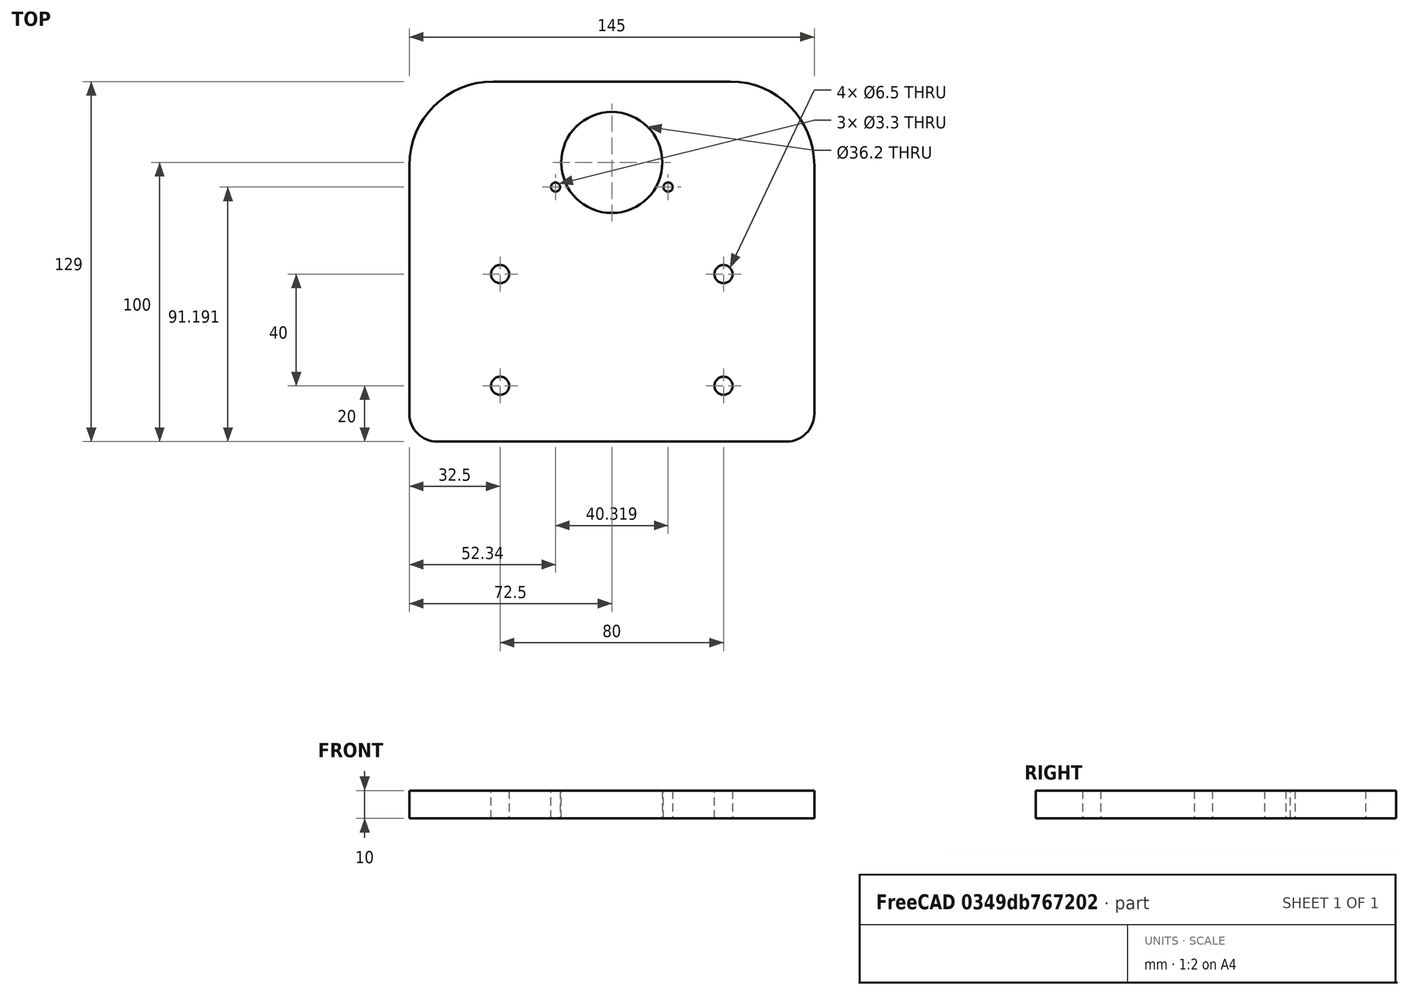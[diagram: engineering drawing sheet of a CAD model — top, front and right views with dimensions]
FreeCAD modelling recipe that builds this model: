
FCSTD DOCUMENT  (FreeCAD 0.21R38887 (Git))
Label: ПластинаY
License: All rights reserved
LicenseURL: http://en.wikipedia.org/wiki/All_rights_reserved
objects: App::Link×2, Sketcher::SketchObject×1, PartDesign::Pad×1, PartDesign::Body×1
note: 6 computed .brp shape members not serialized (recipe doc carries the construction recipe); baked Part::Feature solids carry a one-line shape summary decoded from their .brp
EXTERNAL_REF file=../../../ТаблицаПараметров.FCStd obj=Spreadsheet
EXTERNAL_REF file=../../../ТаблицаПараметров.FCStd obj=Spreadsheet007

FEATURE [Sketcher::SketchObject] Sketch001
  ArcFitTolerance = 0
  ExternalBSplineMaxDegree = 0
  ExternalBSplineTolerance = 0
  FullyConstrained = false
  InternalTolerance = 1e-06
  InvalidShape = false
  MakeInternals = false
  TreeRank = 235
  ValidateShape = false
  expr: Constraints[0] = <<Link(ПластиныY)>>.Len1
  expr: Constraints[1] = <<Link(ПластиныY)>>.Heigh1
  expr: Constraints[38] = <<Link(ПластиныY)>>.Heigh2
  expr: Constraints[48] = <<Link001(Профиль)>>.HTpaz1
  expr: Constraints[49] = <<Link001(Профиль)>>.HTpaz2
  sketch-geometry (17):
    g0: LineSegment StartX=-72.5 StartY=99 StartZ=0 EndX=-72.5 EndY=10 EndZ=0
    g1: ArcOfCircle CenterX=-62.5 CenterY=10 CenterZ=0 NormalX=0 NormalY=0 NormalZ=1 AngleXU=0 Radius=10 StartAngle=3.14159 EndAngle=4.71239
    g2: LineSegment StartX=-62.5 StartY=3.6e-15 StartZ=0 EndX=62.5 EndY=-2.13e-14 EndZ=0
    g3: ArcOfCircle CenterX=62.5 CenterY=10 CenterZ=0 NormalX=0 NormalY=0 NormalZ=1 AngleXU=0 Radius=10 StartAngle=4.71239 EndAngle=6.28319
    g4: LineSegment StartX=72.5 StartY=10 StartZ=0 EndX=72.5 EndY=99 EndZ=0
    g5: ArcOfCircle CenterX=42.5 CenterY=99 CenterZ=0 NormalX=0 NormalY=0 NormalZ=1 AngleXU=0 Radius=30 StartAngle=0 EndAngle=1.5708
    g6: LineSegment StartX=42.5 StartY=129 StartZ=0 EndX=-42.5 EndY=129 EndZ=0
    g7: ArcOfCircle CenterX=-42.5 CenterY=99 CenterZ=0 NormalX=0 NormalY=0 NormalZ=1 AngleXU=0 Radius=30 StartAngle=1.5708 EndAngle=3.14159
    g8: Circle CenterX=-40 CenterY=60 CenterZ=0 NormalX=0 NormalY=0 NormalZ=-1 AngleXU=0 Radius=3.25
    g9: Circle CenterX=-40 CenterY=20 CenterZ=0 NormalX=0 NormalY=0 NormalZ=-1 AngleXU=0 Radius=3.25
    g10: Circle CenterX=40 CenterY=20 CenterZ=0 NormalX=0 NormalY=0 NormalZ=-1 AngleXU=0 Radius=3.25
    g11: Circle CenterX=40 CenterY=60 CenterZ=0 NormalX=0 NormalY=0 NormalZ=-1 AngleXU=0 Radius=3.25
    g12: Circle CenterX=0 CenterY=100 CenterZ=0 NormalX=0 NormalY=0 NormalZ=-1 AngleXU=0 Radius=18.1
    g13: Circle CenterX=20.1596 CenterY=91.1914 CenterZ=0 NormalX=0 NormalY=0 NormalZ=-1 AngleXU=0 Radius=1.65
    g14: Circle CenterX=-20.1596 CenterY=91.1914 CenterZ=0 NormalX=0 NormalY=0 NormalZ=-1 AngleXU=0 Radius=1.65
    g15: Circle CenterX=20.1596 CenterY=91.1914 CenterZ=0 NormalX=0 NormalY=0 NormalZ=-1 AngleXU=0 Radius=1.65
    g16: Circle [constr] CenterX=0 CenterY=100 CenterZ=0 NormalX=0 NormalY=0 NormalZ=1 AngleXU=0 Radius=22
  constraints (50):
    c: DistanceX(g0,g3) = 145
    c: DistanceY(g1,g6) = 129
    c: Vertical(g0)
    c: Vertical(g4)
    c: Horizontal(g6)
    c: Coincident(g0,g7)
    c: Coincident(g6,g7)
    c: Coincident(g5,g6)
    c: Coincident(g4,g5)
    c: Coincident(g3,g4)
    c: Coincident(g2,g3)
    c: Horizontal(g3,g3)
    c: Vertical(g2,g3)
    c: Coincident(g0,g1)
    c: Coincident(g1,g2)
    c: Vertical(g1,g1)
    c: Horizontal(g0,g1)
    c: Equal(g1,g3)
    c: Equal(g7,g5)
    c: Horizontal(g0,g7)
    c: Vertical(g7,g6)
    c: Vertical(g5,g5)
    c: Horizontal(g5,g4)
    c: Radius(g7) = 30
    c: Radius(g1) = 10
    c: PointOnObject(g2,g-1)
    c: Symmetric(g1,g2,g-2)
    c: Diameter(g12) = 36.2
    c: Diameter(g16) = 44
    c: PointOnObject(g15,g16)
    c: PointOnObject(g13,g16)
    c: Horizontal(g14,g15)
    c: Vertical(g13,g15)
    c: Diameter(g13) = 3.3
    c: Equal(g13,g15)
    c: Equal(g15,g14)
    c: Coincident(g12,g16)
    c: PointOnObject(g12,g-2)
    c: DistanceY(g-1,g12) = 100
    c: DistanceX(g8,g11) = 80
    c: Equal(g8,g9)
    c: Equal(g8,g10)
    c: Equal(g8,g11)
    c: Diameter(g8) = 6.5
    c: Vertical(g8,g9)
    c: Vertical(g11,g10)
    c: Horizontal(g11,g8)
    c: Symmetric(g10,g9,g-2)
    c: DistanceY(g-1,g9) = 20
    c: DistanceY(g-1,g8) = 60
FEATURE [PartDesign::Pad] Pad
  AddSubType = 0
  AlongSketchNormal = false
  AutoTaperInnerAngle = false
  CheckUpToFaceLimits = true
  ClaimChildren = false
  Direction = (0,0,1)
  Fit = 0
  FitJoin = 0
  InnerFit = 0
  InnerFitJoin = 0
  InvalidShape = false
  Length = 10
  Length2 = 100
  Linearize = true
  NewSolid = false
  Profile = -> Sketch001
  Suppress = false
  TaperInnerAngle = 0
  TaperInnerAngleRev = 0
  TreeRank = 236
  Type = 0
  ValidateShape = true
  _ProfileBasedVersion = 1
FEATURE [PartDesign::Body] Body  label="ПластинаY1"
  AutoGroupSolids = false
  ClaimAllChildren = false
  ExportMode = 0
  Group = -> [Sketch001,Pad]
  InvalidShape = false
  Origin = -> Origin
  Tip = -> Pad
  TreeRank = 10
  ValidateShape = false
  _ExportChildren = -> [Pad]
  _GroupVersion = 1
FEATURE [App::Link] Link  label="Link(ПластиныY)"
  AutoLinkLabel = true
  AutoPlacement = true
  LinkedObject = -> <external ../../../ТаблицаПараметров.FCStd>#Spreadsheet007
  SyncGroupVisibility = false
  TreeRank = 237
  _LinkVersion = 1
FEATURE [App::Link] Link001  label="Link001(Профиль)"
  AutoLinkLabel = true
  AutoPlacement = true
  LinkedObject = -> <external ../../../ТаблицаПараметров.FCStd>#Spreadsheet
  SyncGroupVisibility = false
  TreeRank = 238
  _LinkVersion = 1

RESOLVED EXTERNAL PARTS (link-assembly join: the EXTERNAL_REF files above that resolve inside this repo's crawl, each included once):
---- part ../../../ТаблицаПараметров.FCStd = doc fcstd_60ae2dd5e8f4 ----
FCSTD DOCUMENT  (FreeCAD 0.21R38887 (Git))
Label: ТаблицаПараметров
License: All rights reserved
LicenseURL: http://en.wikipedia.org/wiki/All_rights_reserved
objects: Spreadsheet::Sheet×9
EXTERNAL_REF file=ЧастиСтанка/Станина/Деталі/NEMA23.FCStd obj=Assembly

FEATURE [Spreadsheet::Sheet] Spreadsheet  label="Профиль"
  PythonMode = false
  ShowCells = 0
  TreeRank = 1
  cells = A2=ДлинаПрофиля; B2(Dlina)==<<ТаблСтанина>>.ShirinaStaninu; A3=ШагОтверстийСоединения; B3(ShagOtv)=100; A4=ДиаметрОтверстия; B4(DiametrOtvSoed)=4; A6=Перша висота Т пазу; B6(HTpaz1)=20; A7=Друга висота Т пазу; B7(HTpaz2)=60; A8=КоличествоОтвСоединения; B8(HoleNumberSoed)==trunc(Dlina / ShagOtv) - 1; A9=ДлинаМасиваСоед; B9(DlinaMasivaSoed)==ShagOtv * HoleNumberSoed; A10=ОтступОтКрая; B10(OtstupRels)==(Dlina - DlinaMasivaSoed) / 2
FEATURE [Spreadsheet::Sheet] Spreadsheet001  label="ТаблСтанина"
  PythonMode = false
  ShowCells = 0
  TreeRank = 0
  cells = A2=Ширина; B2(ShirinaStaninu)=480; A3=Количество палок профиля; B3(NumberProfileBody)=10; A4=Высота; B4(RazmerProfilja)=80; A5=Глубина; B5(GlubinaStaninu)==RazmerProfilja * NumberProfileBody
FEATURE [Spreadsheet::Sheet] Spreadsheet002  label="Ролик"
  PythonMode = false
  ShowCells = 0
  TreeRank = 1
  cells = A7=Высота под подшипник; B7(dimH3)==dimH1 + dimH2; C7=висота   подш + висота шайби; A8=Длина общая (без шайб); B8(dimL1)=222; C8=Final lenght; A9=ball radius; B9(ball_radius)==(<<Ролик>>.dimD2 / 2 - <<Ролик>>.diamPodsh / 2) / 3; C9=alpha; D9(alpa)==atan(.ball_radius / .ball_pos_radius); A10=R for ball; B10(ball_pos_radius)==(<<Ролик>>.dimD2 / 2 - <<Ролик>>.diamPodsh / 2) / 2 + <<Ролик>>.diamPodsh / 2; C10=number of ball; D10(ball_number)==trunc(360 / (2 * .alpa)); C11=Длинная гайка; G11=Винт; I11=Подшипник; L11=Труба; N11=Шайба; O11=Шпилька; B12=Inner thread; C12=External dim; D12=Thread index; E12=Lenght; F12=ШайбаИндекс; G12=Индекс винта; H12=Длина винта(index); I12=Диам подш; J12=диад внутр подш; K12=Высота подш.; L12=Диам внешн.; M12=Диам внутр.; N12=Высота шайбы; O12=Индекс; A13=DIN6334 table; B13==dbind(РоликY#Assembly.Configuration.All); C13(din6334_D1)==.C14; D13(din6334_Index)==.D14; E13(din6334_Len)==.E14; F13(ShaibaIndex)==.F14; G13(IndexVinta)==.G14; H13(dlinaVintaInd)==.H14; I13(dimD2)==.I14; J13(diamPodsh)==.J14; K13(dimH1)==.K14; L13(dimD1)==.L14; M13(dimD3)==.M14; N13(dimH2)==.N14; O13(ShpilkaIndex)==.O14; B14=M5v1; C14=8; D14=13; E14=15; F14=6; G14=3; H14=2; I14=14; J14=5; K14=5; L14=16; M14=12; N14=1; O14=7; B15=M5v2; C15=8; D15=13; E15=15; F15=6; G15=3; H15=2; I15=16; J15=5; K15=5; L15=18; M15=14; N15=1; O15=7; B16=M6; C16=10; D16=14; E16=18; F16=7; G16=4; H16=2; I16=19; J16=6; K16=6; L16=21.3; M16=16.1; N16=1.6; O16=8; B17=M8; C17=13; D17=16; E17=24; F17=8; G17=5; H17=3; I17=22; J17=8; K17=7; L17=25; M17=19; N17=1.6; O17=9
  expr: cells.Bind.C13.ZZ13 = tuple(.cells, <<C>> + str(hiddenref(РоликY#Assembly.Configuration) + 14), <<ZZ>> + str(hiddenref(РоликY#Assembly.Configuration) + 14))
FEATURE [Spreadsheet::Sheet] Spreadsheet004  label="ЗащитаТабл"
  PythonMode = false
  ShowCells = 0
  TreeRank = 1
  cells = A2=Ширина 1; B2(dimL1)=45; C2=Слева от П прорези (зависит от опоры и толщины пластины крепления опоры); D2=dimL1; E2=задать формулу; A3=Ширина 2; B3(dimL2)==<<ТаблСтанина>>.GlubinaStaninu; C3=П прорезь Зависит от ширины профиля и количества палок + небольшой зазор (0.2мм); D3=dimL2; A4=Ширина 3; B4(dimL3)==ceil((<<NEMA23Table>>.TotalLen + dimR1 * 2 + 5) / 5) * 5 + 10; C4=Справа от П прорези (motor); D4=dimL3; A5=Высота 1; B5(dimH1)==<<ПластиныY>>.Heigh1; C5=Общая высота защиты; D5=dimH1; E5=висота пластин и защити однакові; A6=Высота 2; B6(dimh2)=80; C6=Высота профиля ; D6=dimh2; A7=Радиус 1; B7(dimR1)==<<Ролик>>.dimD1 / 2; C7=Радиус скругления по углам с роликами; D7=dimR1; A8=Радиус 2; B8(dimR2)=2.5; C8=Крепление роликов; D8=dimR2; A9=Радиус 3; B9(dimR3)==<<ПроставкаYТабл>>.DiamOtvZashitu / 2; C9=Крепление защиты(радиус отверстя); D9=dimR3; A10=Радиус 4; B10(dimR4)=3; C10=Скругление в точках прилегания к профилю; D10=dimR4; A11=Высота 3; B11(dimH3)==<<ПроставкаYТабл>>.Tolshina / 2; C11=Высота винтов крепления защиты; D11=dimH3; A12=ЧислоВинтов1; B12(num1)==<<ПроставкаYТабл>>.NumberHoleZashita; C12=Количество винтов крепления защиты; D12=num1; A13=Шаг1; B13(dimL4)==<<ПроставкаYТабл>>.ShagOtvZash; C13=Расстояние между винтами защиты; D13=dimL4; A14=ДлинаМасива1; B14(dimL5)==num1 * dimL4; C14=Растояние между крайними віинтами защиты; D14=dimL5; A15=Отступ1; B15(dimL6)==(dimL2 - dimL5) / 2; C15=Отступ от начала П прорези до первого винта крепления защиты; D15=dimL6; A16=Толщина листа; B16(toldhinZashita)=1.5; D16=toldhinZashita
FEATURE [Spreadsheet::Sheet] Spreadsheet006  label="ШВП"
  PythonMode = false
  ShowCells = 0
  TreeRank = 2
  cells = A1=ШВП Х; A7=ШВП Y; B7=Длина общая; C7=Диаметр под гайку; D7=Длина резьбы под гайку; E7=Длина вала под крепление; F7=Длина вала под муфту; G7=Диаметр вала под муфту; H7=Шаг ШВП; I7=Диаметр ШВП; B8(lenY)=407; C8(diamYval)=12; D8(lenRezbaYval1)=10; E8(lenValY1)=36; F8(lenMuftaY)=10; G8(diamMuftaY)=10; H8(ShagScrewY)=5; I8(diamSrewY)=16; A12=ШВП Z
FEATURE [Spreadsheet::Sheet] Spreadsheet007  label="ПластиныY"
  PythonMode = false
  ShowCells = 0
  TreeRank = 3
  cells = A1=Параметры пластин для крепления мотора; A3=Ширина пластины; B3(Len1)=145; A4=Висота пластини; B4(Heigh1)=129; A5=ШВП висота ; B5(Heigh2)=100
FEATURE [Spreadsheet::Sheet] Spreadsheet005  label="ПроставкаYТабл"
  Body = -1
  Configuration = 3
  PythonMode = false
  ShowCells = 0
  TreeRank = 5
  cells = A1=Наименование; B1=Значение; C1=Описание параметра; D1=Наименование; E1=Значение; F1=Описание; A2=ДлинаОбщая; D2=Количество точек крепления защиты; E2(NumberHoleZashita)=7; A3=Толщина Проставки; B3(Tolshina)=25; D3=Шаг отверстий под защиту; E3(ShagOtvZash)==<<ТаблСтанина>>.GlubinaStaninu / (NumberHoleZashita + 1); A4=Ширина Проставки; B4(Shirina)=35; D4=ДлинаМасиваКрепежаЗащиты; E4(DlinaMasivaZashita)==NumberHoleZashita * ShagOtvZash; A5=Отступ от края(основание); B5(BodyFirstHole)=20; C5=Отступ от центра; D5(OtstupCenter)==<<ТаблСтанина>>.GlubinaStaninu / 2 - BodyFirstHole; A6=ШагОтверстий; B6(ShagOtverastij)=40; A8=КоличествоОтверстий; B8(HoleNumber)==trunc((<<ТаблСтанина>>.GlubinaStaninu - BodyFirstHole) / ShagOtverastij); A9=ДлинаЛинМасива; B9(DlinaMasiva)==ShagOtverastij * HoleNumber; A11=КоличествоОтвРельс; B11(HoleNumberRels)==trunc(<<ТаблСтанина>>.GlubinaStaninu / ShagRelsa) - 1; A12=ДлинаМасиваРельс; B12(DlinaMasivaRels)==ShagRelsa * HoleNumberRels; A13=ОтступОтКраяРельса; B13(OtstupRels)==(<<ТаблСтанина>>.GlubinaStaninu - DlinaMasivaRels) / 2; A15=КрепежПроставки; B15=ДиаметрОтверстияПодВинт; C15=ДиаметрОтверстия подГоловку; D15=ГлубинаОтверстияПодГоловку; B16(Body_holeDiam)==.B18; C16(BodyHoleDiam)==.C18; D16(BodyHoleGlubina)==.D18; A17=M3; B17=3.2; C17=6; D17=3.4; A18=M4; B18=4.3; C18=8; D18=4.6; A19=M5; B19=5.3; C19=10; D19=5.7; A20=M6; B20=6.4; C20=11; D20=6.8; B24=Ширина Рельсы; C24=Глубина Посадки; D24=Шаг отверстий; E24=Крепление рельсы (индекс резьбы); F24=Длина Винта Крепления; G24=ГлубинаОтверстияПодВИнт; B25(ShirinaPaza)==.B28; C25(GlubunaPaza)==.C28; D25(ShagRelsa)==.D28; E25(indexKreplRels)==.E28; F25(DlinaVintaRels)==.F28; G25(GlubinaOtvRels)==.G28; A26=HGH15; B26=15; C26=4.3; D26=60; E26=11; F26=16; G26=6; A27=HGH20; B27=20; C27=4.6; D27=60; E27=13; F27=16; G27=8; A28=HGH25; B28=23; C28=5.5; D28=60; E28=14; F28=20; G28=8; A32=Крепление боковой защиты; C32=Глубина отверстия под резьбу; D32=Диаметр отверстия в пластине защиты; B33(indexZashita)==.B38; C33(GlubinaOtvZashitu)==.C38; D33(DiamOtvZashitu)==.D38; A34=M3x10; B34=9; C34=10; D34=3.2; A35=M3x12; B35=9; C35=12; D35=3.2; A36=M4x10; B36=11; C36=10; D36=4.3; A37=M4x12; B37=11; C37=12; D37=4.3; A38=M5x10; B38=13; C38=10; D38=5.3; A39=M5x12; B39=13; C39=12; D39=5.3
  expr: Body.Enum = cells[<<A40:|>>]
  expr: Configuration.Enum = cells[<<A17:|>>]
FEATURE [Spreadsheet::Sheet] Spreadsheet009  label="NEMA23Table"
  PythonMode = false
  ShowCells = 0
  TreeRank = 6
  cells = A1=Тип Мотора; B1=Длина мотора; C1=Длина Тела мотора; D1=Длина Вала; E1=Відстань між отворами кріплення; F1=Діаметр кріплення мотора; G1=Діаметр посадки мотора; H1=Діаметр отвору для різьби; B3(TotalLen)==.B12; C3(BodyLen)==.C12; D3(DlinaVala)==.D12; E3(DistOtv)=47.14; F3(DiamOtv)=5; G3(PosadkaMotor)=38.1; H3(diamRezba)=4.2; A4=23HD2304; B4=45; C4=22; D4=63.4; A5=23HD3005; B5=54; C5=31; D5=72.4; A6=23HD4004; B6=56; C6=33; D6=74.4; A7=23HD5401; B7=65; C7=42; D7=83.4; A8=23HD6001; B8=76; C8=53; D8=94.4; A9=23HD8434; B9=100; C9=77; D9=118.4; A10=23HD2601; B10=45; C10=22; D10=63.4; A11=23HD6603; B11=76; C11=53; D11=94.4; A12=23HD7801; B12=82; C12=59; D12=100.4
  expr: cells.Bind.B3.D3 = tuple(.cells, <<B>> + str(hiddenref(NEMA23#Assembly.Base_MotorType) + 4), <<D>> + str(hiddenref(NEMA23#Assembly.Base_MotorType) + 4))
FEATURE [Spreadsheet::Sheet] Spreadsheet010  label="Стол"
  PythonMode = false
  ShowCells = 0
  TreeRank = 7
  cells = A1=Стіл; A2=Ширина столу; B2(StolShirina)=300; A3=Довжина стола; B3(StolDovjuna)=200; A4=Висота столу; B4(StolVusota)=29; A6=Поглиблення під боковий захист; B6(StolPazZahust)=9; A7=Ширина поглиблення під захист; B7(StolPazShuruna)=232; A9=Площадка під каретки; A10=Довжина; B10(StolKaretkaDovjuna)=180; A11=Ширина; B11(StolKaretkuShurina)=222; A12=Ширина каретки; B12(KaretkaShirina)=36; A13=Глибина паза під каретку; B13(KaretkaPaz)=3; A15=Паз під опору; A16=Ширина; B16(OporaShiruna)=72; A17=Довжина; B17(OporaDovjuna)=29; A18=Глибина пазу під опору; B18(OporaPaz)=3
